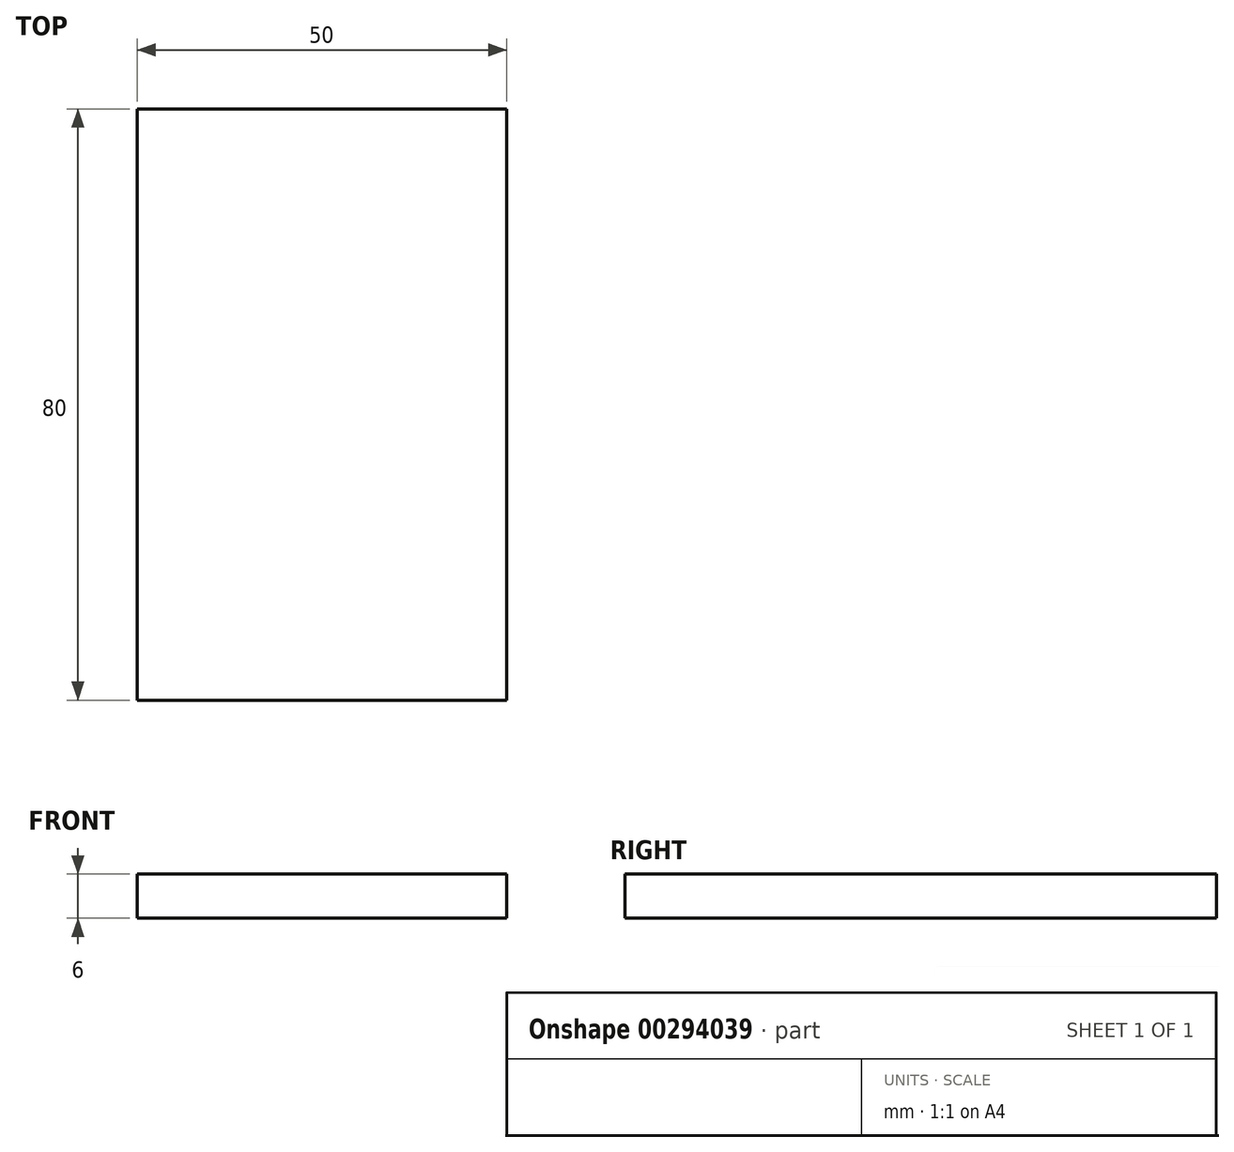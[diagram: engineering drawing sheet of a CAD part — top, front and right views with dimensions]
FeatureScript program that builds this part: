
annotation { "Feature Type Name" : "Feature", "Feature Type Description" : "" }
export const myFeature = defineFeature(function(context is Context, id is Id, definition is map)
    precondition{}
    {
        {
            var Q0;
            Q0=qCreatedBy(makeId("Top.planeOp"),FACE);
            var sketch = newSketch(context, id + "F0", { "sketchPlane" : qUnion([Q0])});
            skLineSegment(sketch, "E0.bottom", {"start": v(-25, 40) * mm, "end": v(25, 40) * mm});
            skLineSegment(sketch, "E0.top", {"start": v(-25, -40) * mm, "end": v(25, -40) * mm});
            skLineSegment(sketch, "E0.left", {"start": v(-25, 40) * mm, "end": v(-25, -40) * mm});
            skLineSegment(sketch, "E0.right", {"start": v(25, 40) * mm, "end": v(25, -40) * mm});
            skPoint(sketch, "E0.middle", {"position": v(0, 0) * mm});
            skSolve(sketch);
        }
        {
            var Q0;
            Q0 = qSketchRegion(id + "F0", true);
            extrude(context, id + "F1", {"entities" : qUnion([Q0]), "depth" : 6 * mm, "offsetDistance" : 25 * mm});
        }
    });
